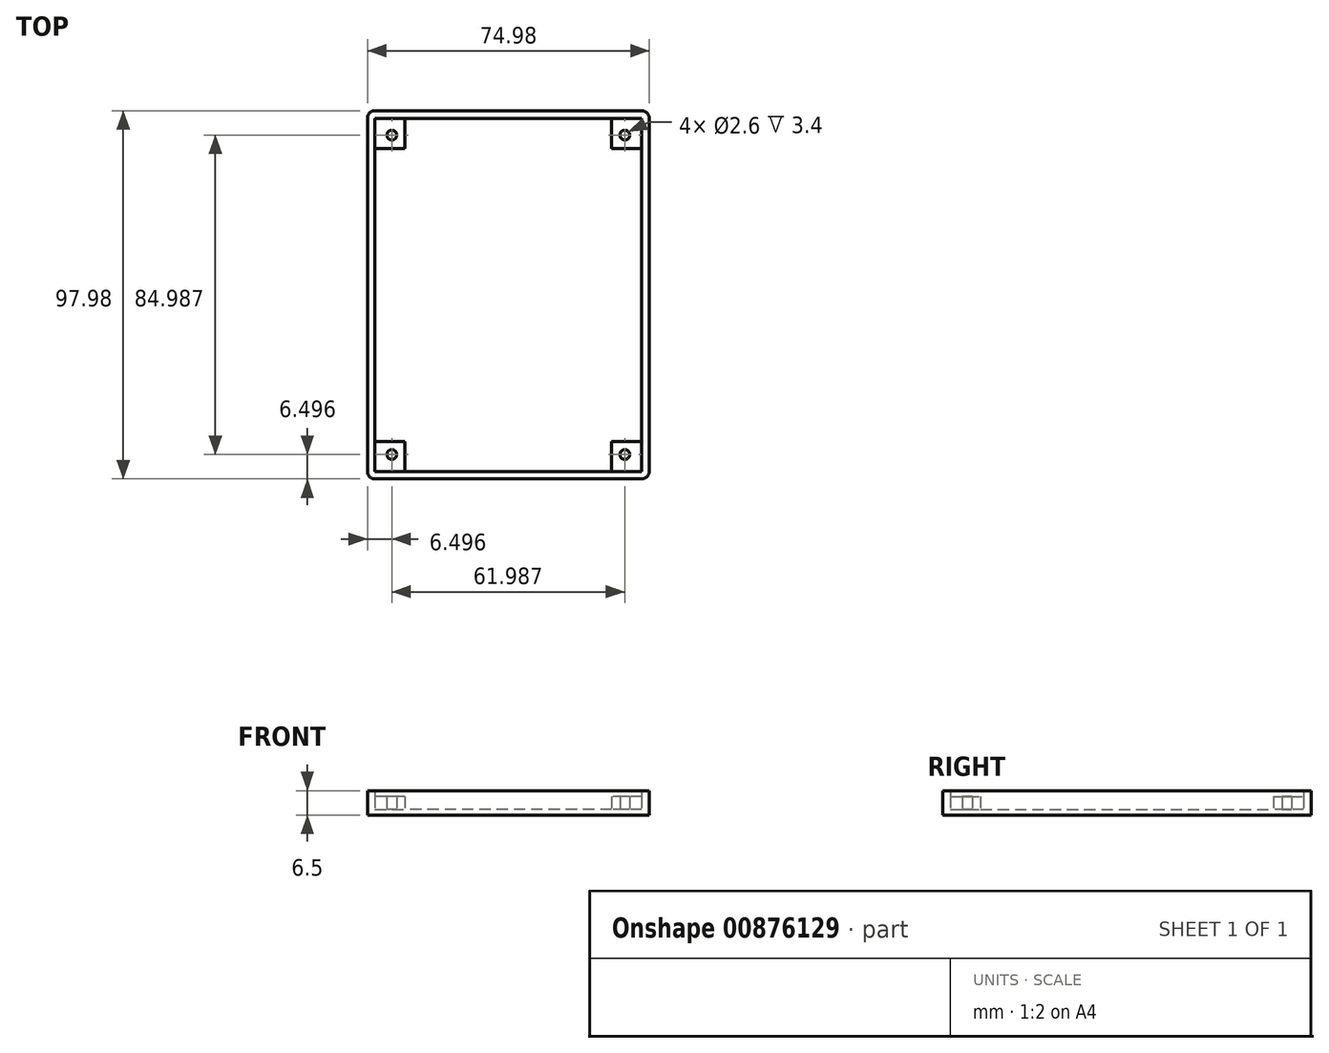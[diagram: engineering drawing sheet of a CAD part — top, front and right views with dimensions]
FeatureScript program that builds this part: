
annotation { "Feature Type Name" : "Feature", "Feature Type Description" : "" }
export const myFeature = defineFeature(function(context is Context, id is Id, definition is map)
    precondition{}
    {
        {
            var Q0;
            Q0=qCreatedBy(makeId("Top.planeOp"),FACE);
            var sketch = newSketch(context, id + "F0", { "sketchPlane" : qUnion([Q0])});
            skLineSegment(sketch, "E0.0", {"start": v(-37, -50.5) * mm, "end": v(-39.5, -50.5) * mm});
            skLineSegment(sketch, "E0.1", {"start": v(-39.5, -47.5) * mm, "end": v(-39.5, -50.5) * mm});
            skLineSegment(sketch, "E0.2", {"start": v(-39.5, -47.5) * mm, "end": v(-39.5, 47.5) * mm});
            skLineSegment(sketch, "E0.3", {"start": v(-37, 47.5) * mm, "end": v(-39.5, 47.5) * mm});
            skLineSegment(sketch, "E0.4", {"start": v(33, 47.5) * mm, "end": v(-37, 47.5) * mm});
            skLineSegment(sketch, "E0.5", {"start": v(-37, -50.5) * mm, "end": v(33, -50.5) * mm});
            skLineSegment(sketch, "E0.6", {"start": v(33, -50.5) * mm, "end": v(35.5, -50.5) * mm});
            skLineSegment(sketch, "E0.7", {"start": v(35.5, -50.5) * mm, "end": v(35.5, -48) * mm});
            skLineSegment(sketch, "E0.8", {"start": v(35.5, -48) * mm, "end": v(35.5, 45) * mm});
            skLineSegment(sketch, "E0.9", {"start": v(35.5, 45) * mm, "end": v(35.5, 47.5) * mm});
            skLineSegment(sketch, "E0.10", {"start": v(35.5, 47.5) * mm, "end": v(33, 47.5) * mm});
            skSolve(sketch);
        }
        {
            var Q0;
            Q0=makeQuery(id+"F0.imprint","IMPRINT",FACE,{"disambiguationData":[TD([[makeQuery(id+"F0.imprint","IMPRINT",EDGE,{"derivedFrom":sQuery(id+"F0.wireOp",EDGE,"E0.0")}),-1.0]])]});
            extrude(context, id + "F1", {"entities" : qUnion([Q0]), "depth" : 1.5 * mm, "offsetDistance" : 25 * mm});
        }
        {
            var Q0;
            Q0=makeQuery(id+"F1.opExtrude","CAP_FACE",FACE,{"disambiguationData":[OSD([sQuery(id+"F0.wireOp",EDGE,"E0.0"),sQuery(id+"F0.wireOp",EDGE,"E0.1"),sQuery(id+"F0.wireOp",EDGE,"E0.2"),sQuery(id+"F0.wireOp",EDGE,"E0.3"),sQuery(id+"F0.wireOp",EDGE,"E0.4"),sQuery(id+"F0.wireOp",EDGE,"E0.5"),sQuery(id+"F0.wireOp",EDGE,"E0.6"),sQuery(id+"F0.wireOp",EDGE,"E0.7"),sQuery(id+"F0.wireOp",EDGE,"E0.8"),sQuery(id+"F0.wireOp",EDGE,"E0.9"),sQuery(id+"F0.wireOp",EDGE,"E0.10")])],"isStart":false});
            var sketch = newSketch(context, id + "F2", { "sketchPlane" : qUnion([Q0])});
            skLineSegment(sketch, "E1.0", {"start": v(33.5, 45.5) * mm, "end": v(-37.5, 45.5) * mm});
            skLineSegment(sketch, "E1.1", {"start": v(33.5, -48.5) * mm, "end": v(33.5, 45.5) * mm});
            skLineSegment(sketch, "E1.2", {"start": v(33.5, -48.5) * mm, "end": v(-37.5, -48.5) * mm});
            skLineSegment(sketch, "E1.3", {"start": v(-37.5, -48.5) * mm, "end": v(-37.5, 45.5) * mm});
            skSolve(sketch);
        }
        {
            var Q0;
            Q0=makeQuery(id+"F2.imprint","IMPRINT",FACE,{"disambiguationData":[TD([[makeQuery(id+"F2.imprint","IMPRINT",EDGE,{"derivedFrom":sQuery(id+"F2.wireOp",EDGE,"E1.0")}),-1.0]])]});
            extrude(context, id + "F3", {"entities" : qUnion([Q0]), "operationType" : NewBodyOperationType.ADD, "depth" : 5 * mm, "offsetDistance" : 25 * mm});
        }
        {
            var Q0;
            Q0=makeQuery(id+"F1.opExtrude","CAP_FACE",FACE,{"disambiguationData":[OSD([sQuery(id+"F0.wireOp",EDGE,"E0.0"),sQuery(id+"F0.wireOp",EDGE,"E0.1"),sQuery(id+"F0.wireOp",EDGE,"E0.2"),sQuery(id+"F0.wireOp",EDGE,"E0.3"),sQuery(id+"F0.wireOp",EDGE,"E0.4"),sQuery(id+"F0.wireOp",EDGE,"E0.5"),sQuery(id+"F0.wireOp",EDGE,"E0.6"),sQuery(id+"F0.wireOp",EDGE,"E0.7"),sQuery(id+"F0.wireOp",EDGE,"E0.8"),sQuery(id+"F0.wireOp",EDGE,"E0.9"),sQuery(id+"F0.wireOp",EDGE,"E0.10")])],"isStart":false});
            var sketch = newSketch(context, id + "F4", { "sketchPlane" : qUnion([Q0])});
            skLineSegment(sketch, "E2.bottom", {"start": v(33.5, 45.5) * mm, "end": v(25.5, 45.5) * mm});
            skLineSegment(sketch, "E2.top", {"start": v(33.5, 37.5) * mm, "end": v(25.5, 37.5) * mm});
            skLineSegment(sketch, "E2.left", {"start": v(33.5, 45.5) * mm, "end": v(33.5, 37.5) * mm});
            skLineSegment(sketch, "E2.right", {"start": v(25.5, 45.5) * mm, "end": v(25.5, 37.5) * mm});
            skLineSegment(sketch, "E3.bottom", {"start": v(-37.5, 45.5) * mm, "end": v(-29.5, 45.5) * mm});
            skLineSegment(sketch, "E3.top", {"start": v(-37.5, 37.5) * mm, "end": v(-29.5, 37.5) * mm});
            skLineSegment(sketch, "E3.left", {"start": v(-37.5, 45.5) * mm, "end": v(-37.5, 37.5) * mm});
            skLineSegment(sketch, "E3.right", {"start": v(-29.5, 45.5) * mm, "end": v(-29.5, 37.5) * mm});
            skLineSegment(sketch, "E4.bottom", {"start": v(-37.5, -48.5) * mm, "end": v(-29.5, -48.5) * mm});
            skLineSegment(sketch, "E4.top", {"start": v(-37.5, -40.5) * mm, "end": v(-29.5, -40.5) * mm});
            skLineSegment(sketch, "E4.left", {"start": v(-37.5, -48.5) * mm, "end": v(-37.5, -40.5) * mm});
            skLineSegment(sketch, "E4.right", {"start": v(-29.5, -48.5) * mm, "end": v(-29.5, -40.5) * mm});
            skLineSegment(sketch, "E5.bottom", {"start": v(33.5, -48.5) * mm, "end": v(25.5, -48.5) * mm});
            skLineSegment(sketch, "E5.top", {"start": v(33.5, -40.5) * mm, "end": v(25.5, -40.5) * mm});
            skLineSegment(sketch, "E5.left", {"start": v(33.5, -48.5) * mm, "end": v(33.5, -40.5) * mm});
            skLineSegment(sketch, "E5.right", {"start": v(25.5, -48.5) * mm, "end": v(25.5, -40.5) * mm});
            skCircle(sketch, "E6", {"center": v(-33, 41) * mm, "radius": 1.3 * mm});
            skCircle(sketch, "E7", {"center": v(29, 41) * mm, "radius": 1.3 * mm});
            skCircle(sketch, "E8", {"center": v(29, -44) * mm, "radius": 1.3 * mm});
            skCircle(sketch, "E9", {"center": v(-33, -44) * mm, "radius": 1.3 * mm});
            skSolve(sketch);
        }
        {
            var Q0;
            Q0=makeQuery(id+"F4.imprint","IMPRINT",FACE,{"disambiguationData":[TD([[makeQuery(id+"F4.imprint","IMPRINT",EDGE,{"derivedFrom":sQuery(id+"F4.wireOp",EDGE,"E3.bottom")}),1.0]])]});
            var Q1;
            Q1=makeQuery(id+"F4.imprint","IMPRINT",FACE,{"disambiguationData":[TD([[makeQuery(id+"F4.imprint","IMPRINT",EDGE,{"derivedFrom":sQuery(id+"F4.wireOp",EDGE,"E2.bottom")}),1.0]])]});
            var Q2;
            Q2=makeQuery(id+"F4.imprint","IMPRINT",FACE,{"disambiguationData":[TD([[makeQuery(id+"F4.imprint","IMPRINT",EDGE,{"derivedFrom":sQuery(id+"F4.wireOp",EDGE,"E5.bottom")}),-1.0]])]});
            var Q3;
            Q3=makeQuery(id+"F4.imprint","IMPRINT",FACE,{"disambiguationData":[TD([[makeQuery(id+"F4.imprint","IMPRINT",EDGE,{"derivedFrom":sQuery(id+"F4.wireOp",EDGE,"E4.bottom")}),-1.0]])]});
            extrude(context, id + "F5", {"entities" : qUnion([Q0, Q1, Q2, Q3]), "operationType" : NewBodyOperationType.ADD, "depth" : (5 - 1.6) * mm, "offsetDistance" : 25 * mm});
        }
        {
            var Q0;
            {var subQ0=sQuery(id+"F0.wireOp",EDGE,"E0.1");var subQ1=sQuery(id+"F0.wireOp",EDGE,"E0.0");Q0=makeQuery(id+"F3.boolean.opBoolean","MERGE",EDGE,{"derivedFrom":[makeQuery(id+"F1.opExtrude","SWEPT_EDGE",EDGE,{"disambiguationData":[OSD([subQ1,subQ0])]}),makeQuery(id+"F3.opExtrude","SWEPT_EDGE",EDGE,{"disambiguationData":[OSD([subQ1,subQ0,sQuery(id+"F0.wireOp",EDGE,"E0.2"),sQuery(id+"F0.wireOp",EDGE,"E0.5"),sQuery(id+"F0.wireOp",EDGE,"E0.6")])]})]});}
            var Q1;
            {var subQ0=sQuery(id+"F0.wireOp",EDGE,"E0.3");var subQ1=sQuery(id+"F0.wireOp",EDGE,"E0.2");Q1=makeQuery(id+"F3.boolean.opBoolean","MERGE",EDGE,{"derivedFrom":[makeQuery(id+"F1.opExtrude","SWEPT_EDGE",EDGE,{"disambiguationData":[OSD([subQ1,subQ0])]}),makeQuery(id+"F3.opExtrude","SWEPT_EDGE",EDGE,{"disambiguationData":[OSD([sQuery(id+"F0.wireOp",EDGE,"E0.1"),subQ1,subQ0,sQuery(id+"F0.wireOp",EDGE,"E0.4"),sQuery(id+"F0.wireOp",EDGE,"E0.10")])]})]});}
            var Q2;
            {var subQ0=sQuery(id+"F0.wireOp",EDGE,"E0.10");var subQ1=sQuery(id+"F0.wireOp",EDGE,"E0.9");Q2=makeQuery(id+"F3.boolean.opBoolean","MERGE",EDGE,{"derivedFrom":[makeQuery(id+"F1.opExtrude","SWEPT_EDGE",EDGE,{"disambiguationData":[OSD([subQ1,subQ0])]}),makeQuery(id+"F3.opExtrude","SWEPT_EDGE",EDGE,{"disambiguationData":[OSD([sQuery(id+"F0.wireOp",EDGE,"E0.3"),sQuery(id+"F0.wireOp",EDGE,"E0.4"),sQuery(id+"F0.wireOp",EDGE,"E0.7"),sQuery(id+"F0.wireOp",EDGE,"E0.8"),subQ1,subQ0])]})]});}
            var Q3;
            {var subQ0=sQuery(id+"F0.wireOp",EDGE,"E0.7");var subQ1=sQuery(id+"F0.wireOp",EDGE,"E0.6");Q3=makeQuery(id+"F3.boolean.opBoolean","MERGE",EDGE,{"derivedFrom":[makeQuery(id+"F1.opExtrude","SWEPT_EDGE",EDGE,{"disambiguationData":[OSD([subQ1,subQ0])]}),makeQuery(id+"F3.opExtrude","SWEPT_EDGE",EDGE,{"disambiguationData":[OSD([sQuery(id+"F0.wireOp",EDGE,"E0.0"),sQuery(id+"F0.wireOp",EDGE,"E0.5"),subQ1,subQ0,sQuery(id+"F0.wireOp",EDGE,"E0.8"),sQuery(id+"F0.wireOp",EDGE,"E0.9")])]})]});}
            fillet(context, id + "F6", {"entities" : qUnion([Q0, Q1, Q2, Q3]), "radius" : 2 * mm, "tangentPropagation" : true, "allowEdgeOverflow" : false});
        }
    });
